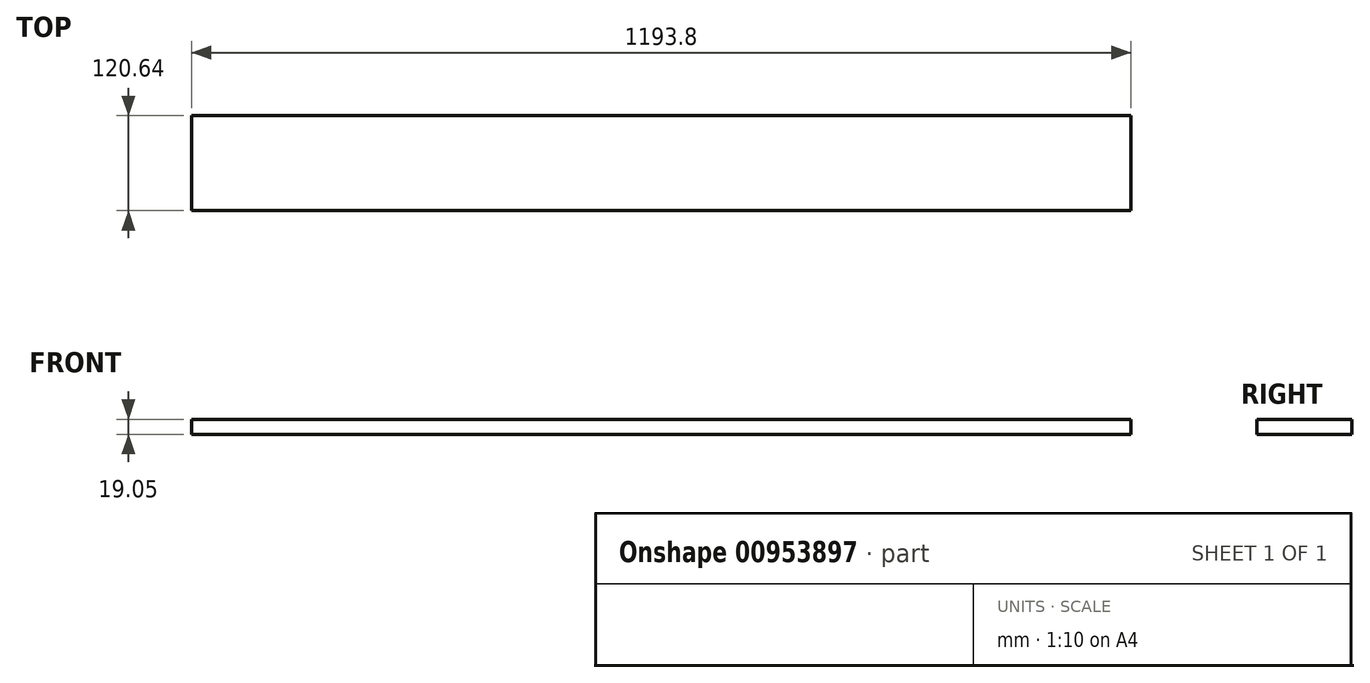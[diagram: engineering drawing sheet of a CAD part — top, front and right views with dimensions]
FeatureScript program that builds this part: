
annotation { "Feature Type Name" : "Feature", "Feature Type Description" : "" }
export const myFeature = defineFeature(function(context is Context, id is Id, definition is map)
    precondition{}
    {
        {
            var Q0;
            Q0=qCreatedBy(makeId("Top.planeOp"),FACE);
            var sketch = newSketch(context, id + "F0", { "sketchPlane" : qUnion([Q0])});
            skLineSegment(sketch, "E0.bottom", {"start": v(596.9, 60.33) * mm, "end": v(-596.9, 60.33) * mm});
            skLineSegment(sketch, "E0.top", {"start": v(596.9, -60.33) * mm, "end": v(-596.9, -60.33) * mm});
            skLineSegment(sketch, "E0.left", {"start": v(596.9, 60.33) * mm, "end": v(596.9, -60.33) * mm});
            skLineSegment(sketch, "E0.right", {"start": v(-596.9, 60.33) * mm, "end": v(-596.9, -60.33) * mm});
            skPoint(sketch, "E0.middle", {"position": v(0, 0) * mm});
            skSolve(sketch);
        }
        {
            var Q0;
            Q0 = qSketchRegion(id + "F0", true);
            extrude(context, id + "F1", {"entities" : qUnion([Q0]), "depth" : 19.05 * mm, "offsetDistance" : 25.4 * mm});
        }
    });
